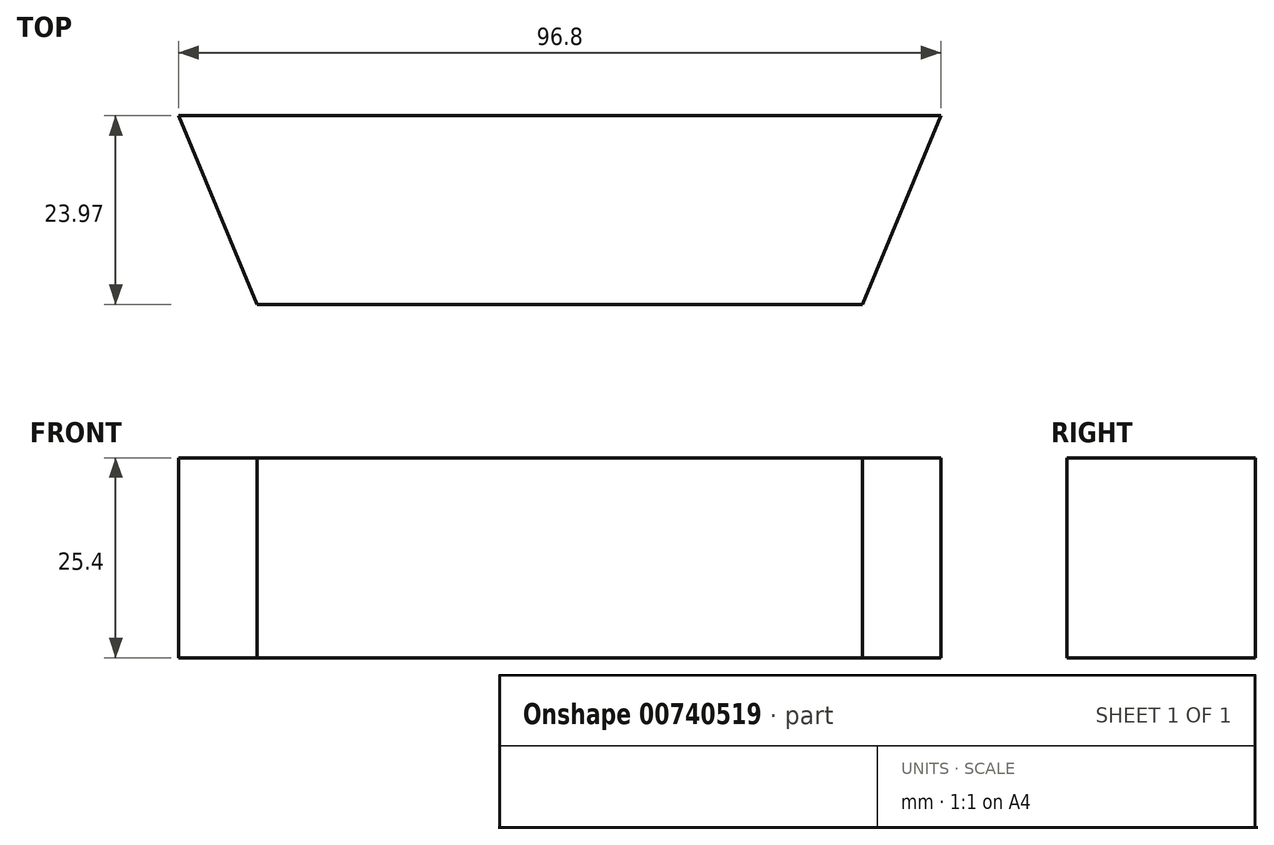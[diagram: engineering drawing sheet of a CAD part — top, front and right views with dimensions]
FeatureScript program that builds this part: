
annotation { "Feature Type Name" : "Feature", "Feature Type Description" : "" }
export const myFeature = defineFeature(function(context is Context, id is Id, definition is map)
    precondition{}
    {
        {
            var Q0;
            Q0=qCreatedBy(makeId("Top.planeOp"),FACE);
            var sketch = newSketch(context, id + "F0", { "sketchPlane" : qUnion([Q0])});
            skLineSegment(sketch, "E0", {"start": v(-36.84, 42.97) * mm, "end": v(59.96, 42.97) * mm});
            skLineSegment(sketch, "E1", {"start": v(59.96, 42.97) * mm, "end": v(50.03, 19) * mm});
            skLineSegment(sketch, "E2", {"start": v(50.03, 19) * mm, "end": v(-26.9, 19) * mm});
            skLineSegment(sketch, "E3", {"start": v(-26.9, 19) * mm, "end": v(-36.84, 42.97) * mm});
            skLineSegment(sketch, "E4", {"start": v(-23.28, 19) * mm, "end": v(-73.4, 19) * mm});
            skLineSegment(sketch, "E5", {"start": v(-36.84, 58.16) * mm, "end": v(-36.84, 11.12) * mm});
            skSolve(sketch);
        }
        {
            var Q0;
            Q0=makeQuery(id+"F0.imprint","IMPRINT",FACE,{"disambiguationData":[TD([[makeQuery(id+"F0.imprint","IMPRINT",EDGE,{"derivedFrom":sQuery(id+"F0.wireOp",EDGE,"E0")}),-1.0]])]});
            extrude(context, id + "F1", {"entities" : qUnion([Q0]), "depth" : 25.4 * mm, "offsetDistance" : 25.4 * mm});
        }
    });
